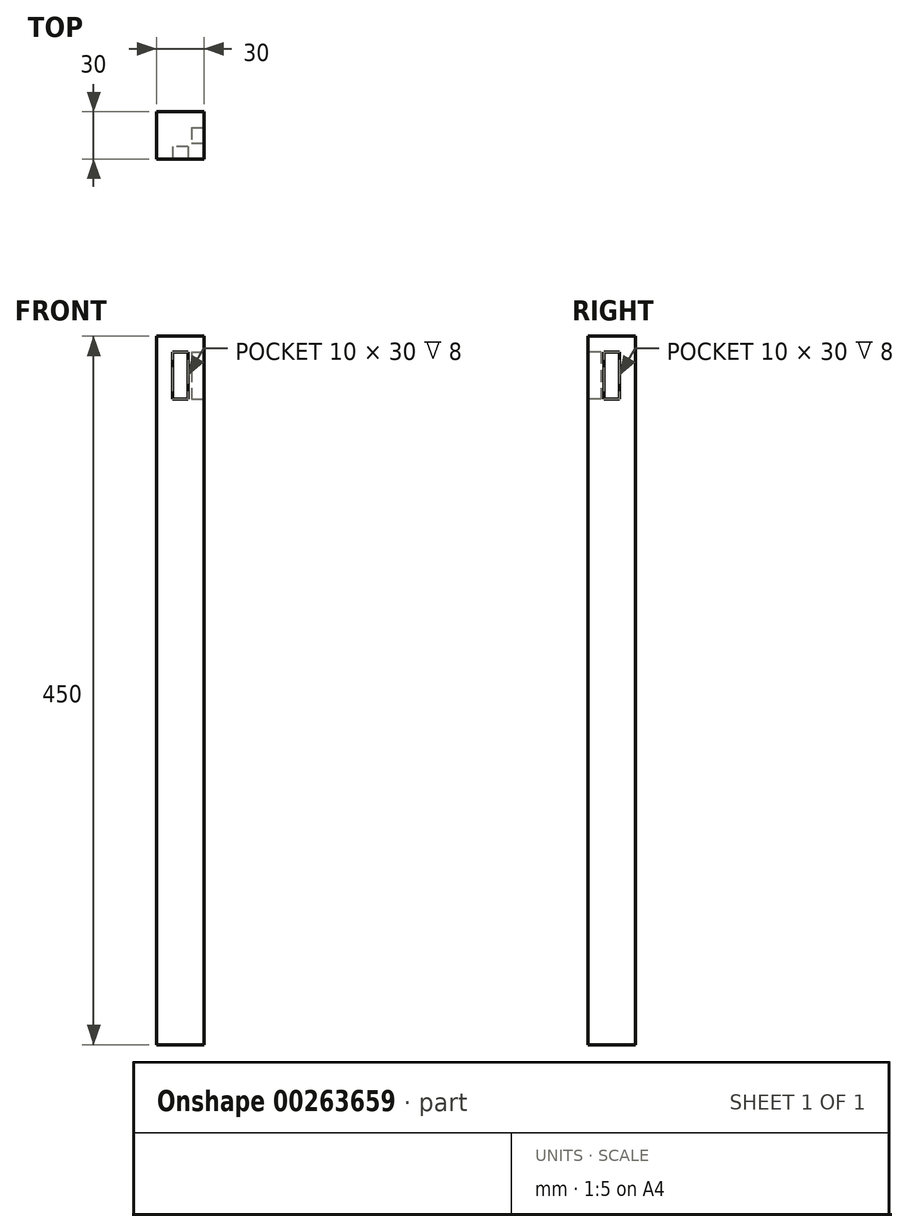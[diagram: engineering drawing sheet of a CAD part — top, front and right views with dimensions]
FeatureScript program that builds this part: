
annotation { "Feature Type Name" : "Feature", "Feature Type Description" : "" }
export const myFeature = defineFeature(function(context is Context, id is Id, definition is map)
    precondition{}
    {
        {
            var Q0;
            Q0=qCreatedBy(makeId("Top.planeOp"),FACE);
            var sketch = newSketch(context, id + "F0", { "sketchPlane" : qUnion([Q0])});
            skLineSegment(sketch, "E0.bottom", {"start": v(0, 0) * mm, "end": v(30, 0) * mm});
            skLineSegment(sketch, "E0.top", {"start": v(0, -30) * mm, "end": v(30, -30) * mm});
            skLineSegment(sketch, "E0.left", {"start": v(0, 0) * mm, "end": v(0, -30) * mm});
            skLineSegment(sketch, "E0.right", {"start": v(30, 0) * mm, "end": v(30, -30) * mm});
            skSolve(sketch);
        }
        {
            var Q0;
            Q0=makeQuery(id+"F0.imprint","IMPRINT",FACE,{"disambiguationData":[TD([[makeQuery(id+"F0.imprint","IMPRINT",EDGE,{"derivedFrom":sQuery(id+"F0.wireOp",EDGE,"E0.bottom")}),-1.0]])]});
            extrude(context, id + "F1", {"entities" : qUnion([Q0]), "depth" : 450 * mm});
        }
        {
            var Q0;
            Q0=makeQuery(id+"F1.opExtrude","SWEPT_FACE",FACE,{"disambiguationData":[OSD([sQuery(id+"F0.wireOp",EDGE,"E0.right")])]});
            var sketch = newSketch(context, id + "F2", { "sketchPlane" : qUnion([Q0])});
            skLineSegment(sketch, "E1.bottom", {"start": v(-10, 440) * mm, "end": v(-20, 440) * mm});
            skLineSegment(sketch, "E1.top", {"start": v(-10, 410) * mm, "end": v(-20, 410) * mm});
            skLineSegment(sketch, "E1.left", {"start": v(-10, 440) * mm, "end": v(-10, 410) * mm});
            skLineSegment(sketch, "E1.right", {"start": v(-20, 440) * mm, "end": v(-20, 410) * mm});
            skSolve(sketch);
        }
        {
            var Q0;
            Q0=qSketchRegion(id+"F2",true);
            extrude(context, id + "F3", {"entities" : qUnion([Q0]), "operationType" : NewBodyOperationType.REMOVE, "oppositeDirection" : true, "depth" : 8 * mm});
        }
        {
            var Q0;
            Q0=makeQuery(id+"F1.opExtrude","SWEPT_FACE",FACE,{"disambiguationData":[OSD([sQuery(id+"F0.wireOp",EDGE,"E0.top")])]});
            var sketch = newSketch(context, id + "F4", { "sketchPlane" : qUnion([Q0])});
            skLineSegment(sketch, "E2.bottom", {"start": v(20, 440) * mm, "end": v(10, 440) * mm});
            skLineSegment(sketch, "E2.top", {"start": v(20, 410) * mm, "end": v(10, 410) * mm});
            skLineSegment(sketch, "E2.left", {"start": v(20, 440) * mm, "end": v(20, 410) * mm});
            skLineSegment(sketch, "E2.right", {"start": v(10, 440) * mm, "end": v(10, 410) * mm});
            skSolve(sketch);
        }
        {
            var Q0;
            Q0=qSketchRegion(id+"F4",true);
            extrude(context, id + "F5", {"entities" : qUnion([Q0]), "operationType" : NewBodyOperationType.REMOVE, "oppositeDirection" : true, "depth" : 8 * mm});
        }
    });
